# Revit family: PRD_FrankeWS_WstBns_STRATOSHygieneWasteBin_STRX611E
name_source: partatom
category: Specialty Equipment
revit_build: Autodesk Revit 2018 (Build: 20190510_1515(x64)
units: mm (PartAtom-declared; Revit-internal decimal feet)

## family parameters
Cut with Voids When Loaded = No
Host = Face
OmniClass Number = 23.40.20.31.11
OmniClass Title = Bins
Part Type = Normal
Room Calculation Point = No
Round Connector Dimension = Use Diameter
Shared = No

## types (1)
- STRX611E
    AssetType = Fixed
    BIMObjectName = PRD_AR_WasteBins_STRATOSHygieneWasteBin_STRX611E
    BagHolder = No
    Category = Pr_40_50_07_96, Waste bins
    Default Elevation = 850 mm  [stored 2.78871 ft]
    Description = Sanitary towel and disposal bin for recessed mounting, stainless steel, surface satin finished, front with InoxPlus surface refinement for the reduction of finger marks and better cleaning characteristics (easy to clean), material thickness 1.5 mm, curved front cover, approx. 3.8 liter capacity, folding selfclosing lid with piano hindge, removable plastic container inside, includes stainless steel screws and dowels.
    DurationUnit = year
    Features = stainless steel, surface satin finished
    FillingVolume = 3.80 liter
    Finish = satin finished
    GrossWeight = 4.71 kg
    IfcExportAs = IfcFurnitureType
    IfcExportType = USERDEFINED
    IntegralAccessories = incl. stainless steel screws and dowels
    IsBuiltIn = TRUE
    Lid = Yes
    Lock = No lock
    MainColor = stainless steel
    Manufacturer = KWC Group AG
    ManufacturerName = KWC Group AG
    ManufacturerURL = www.kwc.com
    Material = stainless steel
    MaterialCode = 1.4301
    MaterialThickness = 1.50 mm
    Model = STRX611E
    ModelNumber = 2000057376
    ModelOffset = 77 mm  [stored 0.252625 ft]
    ModelReference = STRX611E
    NBSDescription = Waste bins
    NBSReference = 45-35-72/380
    Name = Hygiene Waste Bin STRX611E
    NetWeight = 4.12 kg
    NominalDepth = 135 mm  [stored 0.442913 ft]
    NominalHeight = 331 mm  [stored 1.08596 ft]
    NominalWidth = 232 mm  [stored 0.761155 ft]
    ProductInformation = https://pim.kwc.com
    Size = 232 x 331 x 135 mm
    SurfaceTreatment = InoxPlus (anti fingerprint)
    TypeOfFixing = Screw
    TypeOfMounting = Recessed mounting
    URL = www.kwc.com
    Uniclass2015Code = Pr_40_50_07_96
    Uniclass2015Title = Waste bins
    Uniclass2015Version = Products v1.10
    Version = 1
    WarrantyDurationUnit = year
    WasteBinMaterial = PRD_AR_StainlessSteel_SatinFinished

note: [stored X ft] marks values corroborated as IEEE doubles in the binary element streams (Revit-internal decimal feet)

## geometry (parser evidence)
native form markers: Sweep x4
no freeform markers — native parametric forms only
